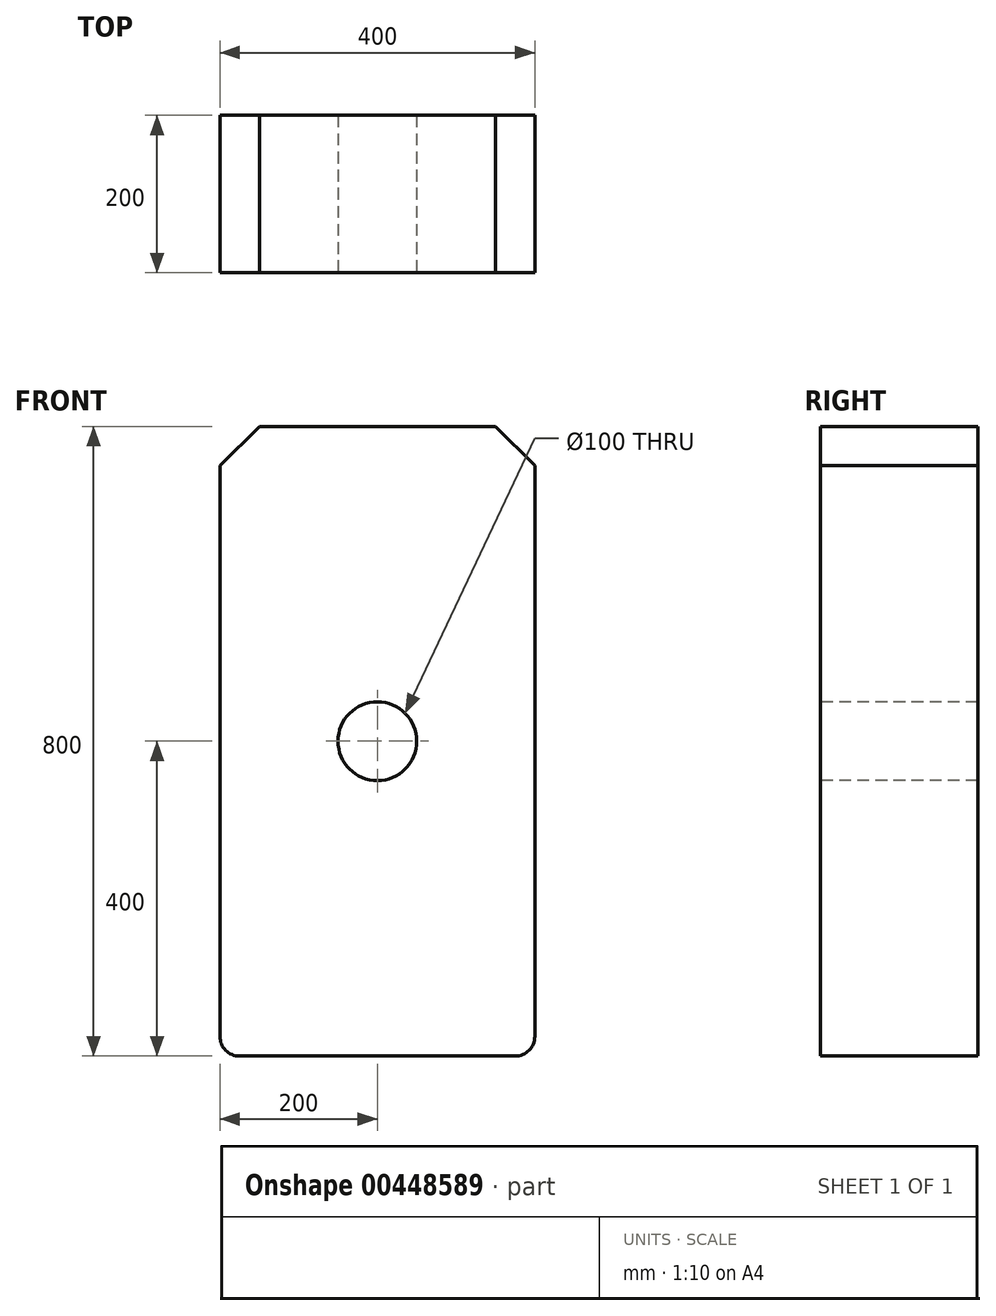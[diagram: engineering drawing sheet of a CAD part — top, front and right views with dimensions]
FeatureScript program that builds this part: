
annotation { "Feature Type Name" : "Feature", "Feature Type Description" : "" }
export const myFeature = defineFeature(function(context is Context, id is Id, definition is map)
    precondition{}
    {
        {
            var Q0;
            Q0=qCreatedBy(makeId("Front.planeOp"),FACE);
            var sketch = newSketch(context, id + "F0", { "sketchPlane" : qUnion([Q0])});
            skLineSegment(sketch, "E0.bottom", {"start": v(200, 400) * mm, "end": v(-200, 400) * mm});
            skLineSegment(sketch, "E0.top", {"start": v(200, -400) * mm, "end": v(-200, -400) * mm});
            skLineSegment(sketch, "E0.left", {"start": v(200, 400) * mm, "end": v(200, -400) * mm});
            skLineSegment(sketch, "E0.right", {"start": v(-200, 400) * mm, "end": v(-200, -400) * mm});
            skPoint(sketch, "E0.middle", {"position": v(0, 0) * mm});
            skSolve(sketch);
        }
        {
            var Q0;
            Q0=makeQuery(id+"F0.imprint","IMPRINT",FACE,{"disambiguationData":[TD([[makeQuery(id+"F0.imprint","IMPRINT",EDGE,{"derivedFrom":sQuery(id+"F0.wireOp",EDGE,"E0.bottom")}),1.0]])]});
            extrude(context, id + "F1", {"entities" : qUnion([Q0]), "depth" : 200 * mm});
        }
        {
            var Q0;
            Q0=makeQuery(id+"F1.opExtrude","SWEPT_EDGE",EDGE,{"disambiguationData":[OSD([sQuery(id+"F0.wireOp",EDGE,"E0.bottom"),sQuery(id+"F0.wireOp",EDGE,"E0.left")])]});
            var Q1;
            Q1=makeQuery(id+"F1.opExtrude","SWEPT_EDGE",EDGE,{"disambiguationData":[OSD([sQuery(id+"F0.wireOp",EDGE,"E0.bottom"),sQuery(id+"F0.wireOp",EDGE,"E0.right")])]});
            chamfer(context, id + "F2", {"entities" : qUnion([Q0, Q1]), "width" : 50 * mm, "tangentPropagation" : true});
        }
        {
            var Q0;
            Q0=makeQuery(id+"F1.opExtrude","SWEPT_EDGE",EDGE,{"disambiguationData":[OSD([sQuery(id+"F0.wireOp",EDGE,"E0.top"),sQuery(id+"F0.wireOp",EDGE,"E0.right")])]});
            var Q1;
            Q1=makeQuery(id+"F1.opExtrude","SWEPT_EDGE",EDGE,{"disambiguationData":[OSD([sQuery(id+"F0.wireOp",EDGE,"E0.top"),sQuery(id+"F0.wireOp",EDGE,"E0.left")])]});
            fillet(context, id + "F3", {"entities" : qUnion([Q0, Q1]), "radius" : 25 * mm, "tangentPropagation" : true, "allowEdgeOverflow" : false});
        }
        {
            var Q0;
            Q0=makeQuery(id+"F1.opExtrude","CAP_FACE",FACE,{"disambiguationData":[OSD([sQuery(id+"F0.wireOp",EDGE,"E0.bottom"),sQuery(id+"F0.wireOp",EDGE,"E0.top"),sQuery(id+"F0.wireOp",EDGE,"E0.left"),sQuery(id+"F0.wireOp",EDGE,"E0.right")])],"isStart":false});
            var sketch = newSketch(context, id + "F4", { "sketchPlane" : qUnion([Q0])});
            skCircle(sketch, "E1", {"center": v(0, 0) * mm, "radius": 50 * mm});
            skSolve(sketch);
        }
        {
            var Q0;
            Q0=makeQuery(id+"F4.imprint","IMPRINT",FACE,{"disambiguationData":[TD([[makeQuery(id+"F4.imprint","IMPRINT",EDGE,{"derivedFrom":sQuery(id+"F4.wireOp",EDGE,"E1")}),1.0]])]});
            extrude(context, id + "F5", {"entities" : qUnion([Q0]), "operationType" : NewBodyOperationType.REMOVE, "endBound" : BoundingType.THROUGH_ALL, "oppositeDirection" : true, "depth" : 25 * mm});
        }
    });
